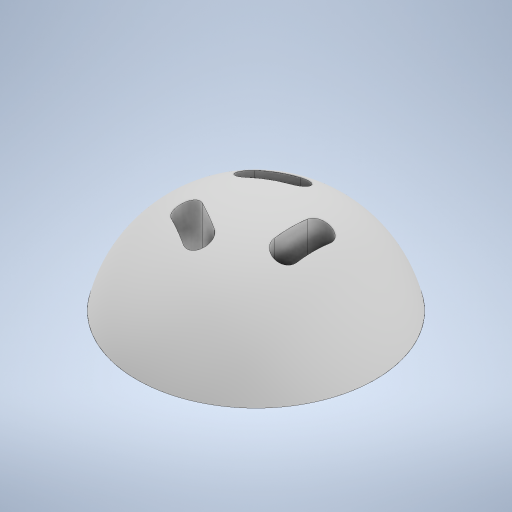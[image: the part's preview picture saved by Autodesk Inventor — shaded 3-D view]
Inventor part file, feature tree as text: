
AUTODESK INVENTOR PART (.ipt)
format: ipt  version: 2024.2 (Build 282272000, 272)  size: 316,416 bytes
history: native  units: mm
features: extrude x3, sketch x2, other x1, revolve x1
ambient origin geometry x8: Origin, YZ Plane, XZ Plane, XY Plane, X Axis, Y Axis, Z Axis, Center Point
bodies: Body1 (feature_tree)
feature tree (7):
  other  "Bryła1"
  sketch  "Szkic1"
  revolve  "Obrót1"
  extrude  "Wyciągnięcie proste1"  Depth=28.2mm
  extrude  "Wyciągnięcie proste2"  Depth=3.5mm
  extrude  "Wyciągnięcie proste3"  Depth=6.981317mm
  sketch  "Szkic3"
